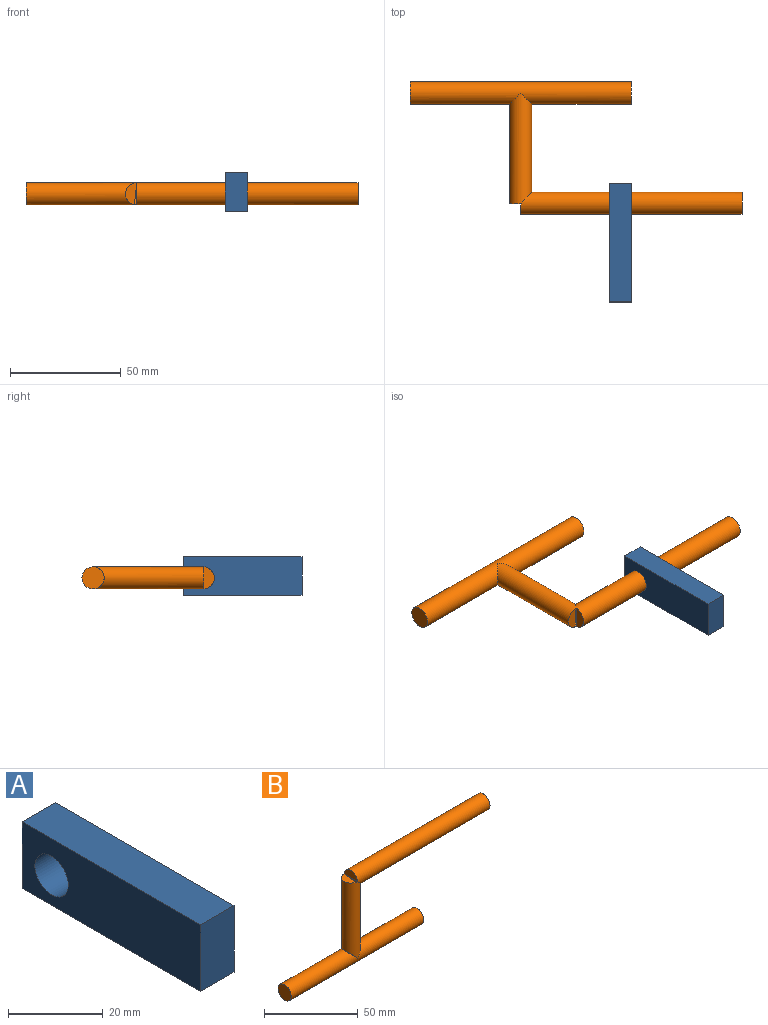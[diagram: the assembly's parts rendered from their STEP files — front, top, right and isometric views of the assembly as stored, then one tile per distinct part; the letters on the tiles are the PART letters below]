
ASSEMBLY  parts=2 mates=1
PART A: 7 faces, bbox 10x53.5x17.2 mm
  f0: plane 53.45x10mm, normal (0,0,1), area 534.5mm2, adj f1,f4,f5,f6
  f1: plane 17.24x10mm, normal (0,-1,0), area 172.4mm2, adj f0,f2,f5,f6
  f2: plane 53.45x10mm, normal (0,0,-1), area 534.5mm2, adj f1,f4,f5,f6
  f3: cylinder r=5mm len=10mm, axis (1,0,0), area 314.2mm2, adj f5,f6
  f4: plane 17.24x10mm, normal (0,1,0), area 172.4mm2, adj f0,f2,f5,f6
  f5: plane 53.45x17.24mm, normal (-1,0,0), area 843mm2, adj f0,f1,f2,f3,f4
  f6: plane 53.45x17.24mm, normal (1,0,0), area 843mm2, adj f0,f1,f2,f3,f4
PART B: 9 faces, bbox 150x10x59.8 mm
  f0: cylinder r=5mm len=50mm, axis (0,0,-1), area 1417.5mm2, adj f1,f2,f3,f6
  f1: cylinder r=5mm len=0.21mm, axis (0,0,-1), area 0mm2, adj f0,f2,f6
  f2: plane 10x5.21mm, normal (0,0,1), area 39.3mm2, adj f0,f1,f6,f8
  f3: cylinder r=5mm len=100mm, axis (-1,0,0), area 3041.6mm2, adj f0,f4,f5
  f4: plane 10x10mm, normal (1,0,0), area 78.5mm2, adj f3
  f5: plane 10x10mm, normal (-1,0,0), area 78.5mm2, adj f3
  f6: cylinder r=5mm len=100mm, axis (-1,0,0), area 3091.5mm2, adj f0,f1,f2,f7,f8
  f7: plane 10x10mm, normal (1,0,0), area 78.5mm2, adj f6
  f8: plane 9.99x4.79mm, normal (-1,0,0), area 37.1mm2, adj f2,f6
PLACE A t=(-119.25,-38.1,-18.66)mm
PLACE B rot(axis=(1,0,0),90deg) t=(-69.25,11.69,31.12)mm
MATE revolute B.f6 <-> A.f3  axis (-1,0,0) through (-19.25,-38.1,31.12)mm
